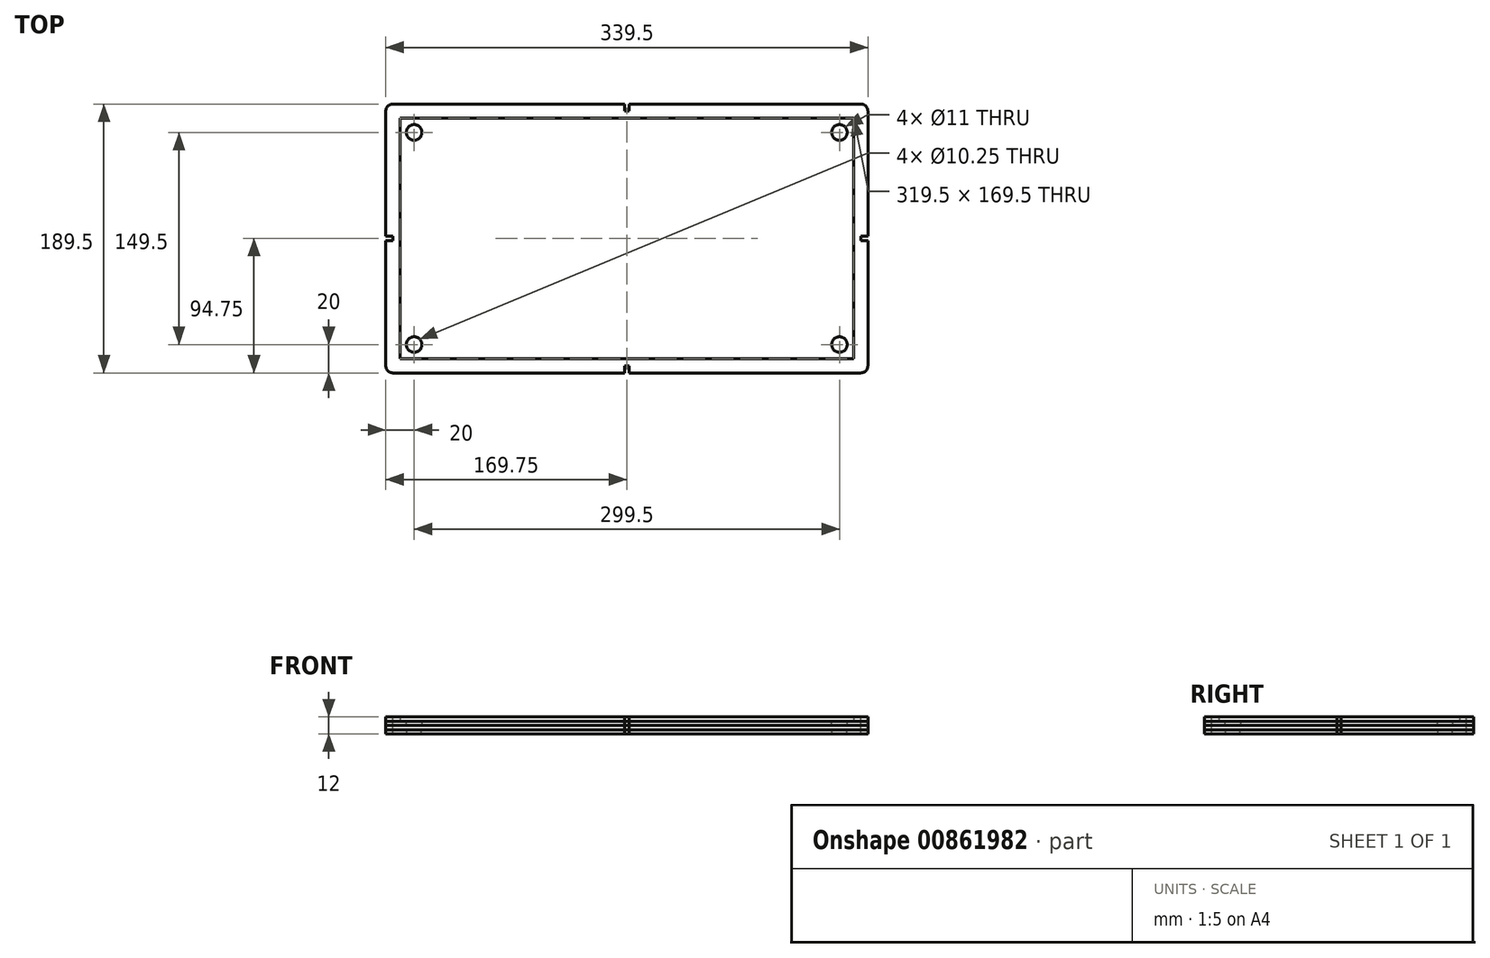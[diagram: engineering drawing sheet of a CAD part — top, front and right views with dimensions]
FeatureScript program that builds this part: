
annotation { "Feature Type Name" : "Feature", "Feature Type Description" : "" }
export const myFeature = defineFeature(function(context is Context, id is Id, definition is map)
    precondition{}
    {
        {
            var Q0;
            Q0=qCreatedBy(makeId("Top.planeOp"),FACE);
            var sketch = newSketch(context, id + "F0", { "sketchPlane" : qUnion([Q0])});
            skLineSegment(sketch, "E0.bottom", {"start": v(-158.75, 83.75) * mm, "end": v(158.75, 83.75) * mm});
            skLineSegment(sketch, "E0.top", {"start": v(-158.75, -83.75) * mm, "end": v(158.75, -83.75) * mm});
            skLineSegment(sketch, "E0.left", {"start": v(-158.75, 83.75) * mm, "end": v(-158.75, -83.75) * mm});
            skLineSegment(sketch, "E0.right", {"start": v(158.75, 83.75) * mm, "end": v(158.75, -83.75) * mm});
            skPoint(sketch, "E0.middle", {"position": v(0, 0) * mm});
            skLineSegment(sketch, "E1.bottom", {"start": v(-149.75, 74.75) * mm, "end": v(149.75, 74.75) * mm, "construction": true});
            skLineSegment(sketch, "E1.top", {"start": v(-149.75, -74.75) * mm, "end": v(149.75, -74.75) * mm, "construction": true});
            skLineSegment(sketch, "E1.left", {"start": v(-149.75, 74.75) * mm, "end": v(-149.75, -74.75) * mm, "construction": true});
            skLineSegment(sketch, "E1.right", {"start": v(149.75, 74.75) * mm, "end": v(149.75, -74.75) * mm, "construction": true});
            skCircle(sketch, "E2", {"center": v(-149.75, 74.75) * mm, "radius": 6 * mm});
            skCircle(sketch, "E3", {"center": v(149.75, 74.75) * mm, "radius": 6 * mm});
            skCircle(sketch, "E4", {"center": v(149.75, -74.75) * mm, "radius": 6 * mm});
            skCircle(sketch, "E5", {"center": v(-149.75, -74.75) * mm, "radius": 6 * mm});
            skSolve(sketch);
        }
        {
            var Q0;
            Q0=makeQuery(id+"F0.imprint","IMPRINT",FACE,{"disambiguationData":[TD([[makeQuery(id+"F0.imprint","IMPRINT",EDGE,{"derivedFrom":sQuery(id+"F0.wireOp",EDGE,"E0.bottom")}),-1.0]])]});
            var sketch = newSketch(context, id + "F1", { "sketchPlane" : qUnion([Q0])});
            skLineSegment(sketch, "E6.0", {"start": v(-159.75, 84.75) * mm, "end": v(-159.75, -84.75) * mm});
            skLineSegment(sketch, "E6.1", {"start": v(159.75, 84.75) * mm, "end": v(-159.75, 84.75) * mm});
            skLineSegment(sketch, "E6.2", {"start": v(159.75, -84.75) * mm, "end": v(159.75, 84.75) * mm});
            skLineSegment(sketch, "E6.3", {"start": v(-159.75, -84.75) * mm, "end": v(159.75, -84.75) * mm});
            skLineSegment(sketch, "E7.bottom", {"start": v(164.75, 94.75) * mm, "end": v(-164.75, 94.75) * mm});
            skLineSegment(sketch, "E7.top", {"start": v(164.75, -94.75) * mm, "end": v(-164.75, -94.75) * mm});
            skLineSegment(sketch, "E7.left", {"start": v(169.75, 89.75) * mm, "end": v(169.75, -89.75) * mm});
            skLineSegment(sketch, "E7.right", {"start": v(-169.75, 89.75) * mm, "end": v(-169.75, -89.75) * mm});
            skPoint(sketch, "E7.middle", {"position": v(0, 0) * mm});
            skPoint(sketch, "E8.visualSharp", {"position": v(169.75, 94.75) * mm});
            skArc(sketch, "E8.filletArc", {"start": v(169.75, 89.75) * mm, "mid": v(168.29, 93.29) * mm, "end": v(164.75, 94.75) * mm});
            skPoint(sketch, "E9.visualSharp", {"position": v(169.75, -94.75) * mm});
            skArc(sketch, "E9.filletArc", {"start": v(164.75, -94.75) * mm, "mid": v(168.29, -93.29) * mm, "end": v(169.75, -89.75) * mm});
            skPoint(sketch, "E10.visualSharp", {"position": v(-169.75, -94.75) * mm});
            skArc(sketch, "E10.filletArc", {"start": v(-169.75, -89.75) * mm, "mid": v(-168.29, -93.29) * mm, "end": v(-164.75, -94.75) * mm});
            skPoint(sketch, "E11.visualSharp", {"position": v(-169.75, 94.75) * mm});
            skArc(sketch, "E11.filletArc", {"start": v(-164.75, 94.75) * mm, "mid": v(-168.29, 93.29) * mm, "end": v(-169.75, 89.75) * mm});
            skSolve(sketch);
        }
        {
            var Q0;
            Q0 = qSketchRegion(id + "F1", true);
            extrude(context, id + "F2", {"entities" : qUnion([Q0]), "depth" : 3 * mm, "offsetDistance" : 25 * mm});
        }
        {
            var Q0;
            Q0=makeQuery(id+"F2.opExtrude","CAP_FACE",FACE,{"disambiguationData":[OSD([sQuery(id+"F1.wireOp",EDGE,"E6.0"),sQuery(id+"F1.wireOp",EDGE,"E6.1"),sQuery(id+"F1.wireOp",EDGE,"E6.2"),sQuery(id+"F1.wireOp",EDGE,"E6.3"),sQuery(id+"F1.wireOp",EDGE,"E7.bottom"),sQuery(id+"F1.wireOp",EDGE,"E7.top"),sQuery(id+"F1.wireOp",EDGE,"E7.left"),sQuery(id+"F1.wireOp",EDGE,"E7.right"),sQuery(id+"F1.wireOp",EDGE,"E8.filletArc"),sQuery(id+"F1.wireOp",EDGE,"E9.filletArc"),sQuery(id+"F1.wireOp",EDGE,"E10.filletArc"),sQuery(id+"F1.wireOp",EDGE,"E11.filletArc")])],"isStart":true});
            var sketch = newSketch(context, id + "F3", { "sketchPlane" : qUnion([Q0])});
            skLineSegment(sketch, "E12.0.0", {"start": v(164.75, 94.75) * mm, "end": v(-164.75, 94.75) * mm});
            skArc(sketch, "E12.0.1", {"start": v(-164.75, 94.75) * mm, "mid": v(-168.29, 93.29) * mm, "end": v(-169.75, 89.75) * mm});
            skLineSegment(sketch, "E12.0.2", {"start": v(-169.75, 89.75) * mm, "end": v(-169.75, -89.75) * mm});
            skArc(sketch, "E12.0.3", {"start": v(-169.75, -89.75) * mm, "mid": v(-168.29, -93.29) * mm, "end": v(-164.75, -94.75) * mm});
            skLineSegment(sketch, "E12.0.4", {"start": v(-164.75, -94.75) * mm, "end": v(164.75, -94.75) * mm});
            skArc(sketch, "E12.0.5", {"start": v(164.75, -94.75) * mm, "mid": v(168.29, -93.29) * mm, "end": v(169.75, -89.75) * mm});
            skLineSegment(sketch, "E12.0.6", {"start": v(169.75, -89.75) * mm, "end": v(169.75, 89.75) * mm});
            skArc(sketch, "E12.0.7", {"start": v(169.75, 89.75) * mm, "mid": v(168.29, 93.29) * mm, "end": v(164.75, 94.75) * mm});
            skCircle(sketch, "E13.0", {"center": v(-149.75, 74.75) * mm, "radius": 5.5 * mm});
            skCircle(sketch, "E14.0", {"center": v(149.75, 74.75) * mm, "radius": 5.5 * mm});
            skCircle(sketch, "E15.0", {"center": v(149.75, -74.75) * mm, "radius": 5.5 * mm});
            skCircle(sketch, "E16.0", {"center": v(-149.75, -74.75) * mm, "radius": 5.5 * mm});
            skSolve(sketch);
        }
        {
            var Q0;
            Q0 = qSketchRegion(id + "F3", true);
            extrude(context, id + "F4", {"entities" : qUnion([Q0]), "depth" : 3 * mm, "offsetDistance" : 25 * mm});
        }
        {
            var Q0;
            Q0=makeQuery(id+"F4.opExtrude","CAP_FACE",FACE,{"disambiguationData":[OSD([sQuery(id+"F3.wireOp",EDGE,"E12.0.0"),sQuery(id+"F3.wireOp",EDGE,"E12.0.1"),sQuery(id+"F3.wireOp",EDGE,"E12.0.2"),sQuery(id+"F3.wireOp",EDGE,"E12.0.3"),sQuery(id+"F3.wireOp",EDGE,"E12.0.4"),sQuery(id+"F3.wireOp",EDGE,"E12.0.5"),sQuery(id+"F3.wireOp",EDGE,"E12.0.6"),sQuery(id+"F3.wireOp",EDGE,"E12.0.7"),sQuery(id+"F3.wireOp",EDGE,"E13.0"),sQuery(id+"F3.wireOp",EDGE,"E14.0"),sQuery(id+"F3.wireOp",EDGE,"E15.0"),sQuery(id+"F3.wireOp",EDGE,"E16.0")])],"isStart":false});
            var sketch = newSketch(context, id + "F5", { "sketchPlane" : qUnion([Q0])});
            skArc(sketch, "E17.0.0", {"start": v(169.75, 89.75) * mm, "mid": v(168.29, 93.29) * mm, "end": v(164.75, 94.75) * mm});
            skLineSegment(sketch, "E17.0.1", {"start": v(164.75, 94.75) * mm, "end": v(-164.75, 94.75) * mm});
            skArc(sketch, "E17.0.2", {"start": v(-164.75, 94.75) * mm, "mid": v(-168.29, 93.29) * mm, "end": v(-169.75, 89.75) * mm});
            skLineSegment(sketch, "E17.0.3", {"start": v(-169.75, 89.75) * mm, "end": v(-169.75, -89.75) * mm});
            skArc(sketch, "E17.0.4", {"start": v(-169.75, -89.75) * mm, "mid": v(-168.29, -93.29) * mm, "end": v(-164.75, -94.75) * mm});
            skLineSegment(sketch, "E17.0.5", {"start": v(-164.75, -94.75) * mm, "end": v(164.75, -94.75) * mm});
            skArc(sketch, "E17.0.6", {"start": v(164.75, -94.75) * mm, "mid": v(168.29, -93.29) * mm, "end": v(169.75, -89.75) * mm});
            skLineSegment(sketch, "E17.0.7", {"start": v(169.75, -89.75) * mm, "end": v(169.75, 89.75) * mm});
            skSolve(sketch);
        }
        {
            var Q0;
            Q0 = qSketchRegion(id + "F5", true);
            extrude(context, id + "F6", {"entities" : qUnion([Q0]), "depth" : 3 * mm, "offsetDistance" : 25 * mm});
        }
        {
            var Q0;
            Q0=makeQuery(id+"F6.opExtrude","CAP_FACE",FACE,{"disambiguationData":[OSD([sQuery(id+"F5.wireOp",EDGE,"E17.0.0"),sQuery(id+"F5.wireOp",EDGE,"E17.0.1"),sQuery(id+"F5.wireOp",EDGE,"E17.0.2"),sQuery(id+"F5.wireOp",EDGE,"E17.0.3"),sQuery(id+"F5.wireOp",EDGE,"E17.0.4"),sQuery(id+"F5.wireOp",EDGE,"E17.0.5"),sQuery(id+"F5.wireOp",EDGE,"E17.0.6"),sQuery(id+"F5.wireOp",EDGE,"E17.0.7")])],"isStart":false});
            var sketch = newSketch(context, id + "F7", { "sketchPlane" : qUnion([Q0])});
            skArc(sketch, "E18.0.0", {"start": v(169.75, 89.75) * mm, "mid": v(168.29, 93.29) * mm, "end": v(164.75, 94.75) * mm});
            skLineSegment(sketch, "E18.0.1", {"start": v(164.75, 94.75) * mm, "end": v(-164.75, 94.75) * mm});
            skArc(sketch, "E18.0.2", {"start": v(-164.75, 94.75) * mm, "mid": v(-168.29, 93.29) * mm, "end": v(-169.75, 89.75) * mm});
            skLineSegment(sketch, "E18.0.3", {"start": v(-169.75, 89.75) * mm, "end": v(-169.75, -89.75) * mm});
            skArc(sketch, "E18.0.4", {"start": v(-169.75, -89.75) * mm, "mid": v(-168.29, -93.29) * mm, "end": v(-164.75, -94.75) * mm});
            skLineSegment(sketch, "E18.0.5", {"start": v(-164.75, -94.75) * mm, "end": v(164.75, -94.75) * mm});
            skArc(sketch, "E18.0.6", {"start": v(164.75, -94.75) * mm, "mid": v(168.29, -93.29) * mm, "end": v(169.75, -89.75) * mm});
            skLineSegment(sketch, "E18.0.7", {"start": v(169.75, -89.75) * mm, "end": v(169.75, 89.75) * mm});
            skCircle(sketch, "E19.0", {"center": v(149.75, -74.75) * mm, "radius": 5.5 * mm, "construction": true});
            skCircle(sketch, "E20.0", {"center": v(-149.75, -74.75) * mm, "radius": 5.5 * mm, "construction": true});
            skCircle(sketch, "E21.0", {"center": v(-149.75, 74.75) * mm, "radius": 5.5 * mm, "construction": true});
            skCircle(sketch, "E22.0", {"center": v(149.75, 74.75) * mm, "radius": 5.5 * mm, "construction": true});
            skCircle(sketch, "E23", {"center": v(-149.75, 74.75) * mm, "radius": 5.12 * mm});
            skCircle(sketch, "E24", {"center": v(149.75, 74.75) * mm, "radius": 5.12 * mm});
            skCircle(sketch, "E25", {"center": v(149.75, -74.75) * mm, "radius": 5.12 * mm});
            skCircle(sketch, "E26", {"center": v(-149.75, -74.75) * mm, "radius": 5.12 * mm});
            skSolve(sketch);
        }
        {
            var Q0;
            Q0 = qSketchRegion(id + "F7", true);
            extrude(context, id + "F8", {"entities" : qUnion([Q0]), "depth" : 3 * mm, "offsetDistance" : 25 * mm});
        }
        {
            var Q0;
            Q0=makeQuery(id+"F2.opExtrude","CAP_FACE",FACE,{"disambiguationData":[OSD([sQuery(id+"F1.wireOp",EDGE,"E6.0"),sQuery(id+"F1.wireOp",EDGE,"E6.1"),sQuery(id+"F1.wireOp",EDGE,"E6.2"),sQuery(id+"F1.wireOp",EDGE,"E6.3"),sQuery(id+"F1.wireOp",EDGE,"E7.bottom"),sQuery(id+"F1.wireOp",EDGE,"E7.top"),sQuery(id+"F1.wireOp",EDGE,"E7.left"),sQuery(id+"F1.wireOp",EDGE,"E7.right"),sQuery(id+"F1.wireOp",EDGE,"E8.filletArc"),sQuery(id+"F1.wireOp",EDGE,"E9.filletArc"),sQuery(id+"F1.wireOp",EDGE,"E10.filletArc"),sQuery(id+"F1.wireOp",EDGE,"E11.filletArc")])],"isStart":false});
            var sketch = newSketch(context, id + "F9", { "sketchPlane" : qUnion([Q0])});
            skPoint(sketch, "E27.endSnap0", {"position": v(0, 84.75) * mm});
            skLineSegment(sketch, "E28.bottom", {"start": v(-1.5, 94.75) * mm, "end": v(1.5, 94.75) * mm});
            skLineSegment(sketch, "E28.top", {"start": v(-1.5, 89.75) * mm, "end": v(1.5, 89.75) * mm});
            skLineSegment(sketch, "E28.left", {"start": v(-1.5, 94.75) * mm, "end": v(-1.5, 89.75) * mm});
            skLineSegment(sketch, "E28.right", {"start": v(1.5, 94.75) * mm, "end": v(1.5, 89.75) * mm});
            skLineSegment(sketch, "E29", {"start": v(0, 89.75) * mm, "end": v(0, 94.75) * mm, "construction": true});
            skLineSegment(sketch, "E30", {"start": v(0, 0) * mm, "end": v(0, 84.75) * mm, "construction": true});
            skLineSegment(sketch, "E31", {"start": v(0, 0) * mm, "end": v(169.75, 0) * mm, "construction": true});
            skLineSegment(sketch, "E32.MirrorCS", {"start": v(1.5, 89.75) * mm, "end": v(-1.5, 89.75) * mm});
            skLineSegment(sketch, "E33.MirrorCS", {"start": v(1.5, 94.75) * mm, "end": v(-1.5, 94.75) * mm});
            skLineSegment(sketch, "E34.MirrorCS", {"start": v(1.5, -94.75) * mm, "end": v(-1.5, -94.75) * mm});
            skLineSegment(sketch, "E35.MirrorCS", {"start": v(1.5, -89.75) * mm, "end": v(-1.5, -89.75) * mm});
            skLineSegment(sketch, "E36.MirrorCS", {"start": v(-1.5, -94.75) * mm, "end": v(1.5, -94.75) * mm});
            skLineSegment(sketch, "E37.MirrorCS", {"start": v(1.5, -94.75) * mm, "end": v(1.5, -89.75) * mm});
            skLineSegment(sketch, "E38.MirrorCS", {"start": v(-1.5, -89.75) * mm, "end": v(1.5, -89.75) * mm});
            skLineSegment(sketch, "E39.MirrorCS", {"start": v(-1.5, -94.75) * mm, "end": v(-1.5, -89.75) * mm});
            skLineSegment(sketch, "E40.MirrorCS", {"start": v(0, -89.75) * mm, "end": v(0, -94.75) * mm, "construction": true});
            skLineSegment(sketch, "E41.bottom", {"start": v(169.75, -1.5) * mm, "end": v(164.75, -1.5) * mm});
            skLineSegment(sketch, "E41.top", {"start": v(169.75, 1.5) * mm, "end": v(164.75, 1.5) * mm});
            skLineSegment(sketch, "E41.left", {"start": v(169.75, -1.5) * mm, "end": v(169.75, 1.5) * mm});
            skLineSegment(sketch, "E41.right", {"start": v(164.75, -1.5) * mm, "end": v(164.75, 1.5) * mm});
            skPoint(sketch, "E42", {"position": v(164.75, 0) * mm});
            skLineSegment(sketch, "E43.MirrorCS", {"start": v(-169.75, -1.5) * mm, "end": v(-169.75, 1.5) * mm});
            skLineSegment(sketch, "E44.MirrorCS", {"start": v(-164.75, -1.5) * mm, "end": v(-164.75, 1.5) * mm});
            skLineSegment(sketch, "E45.MirrorCS", {"start": v(-169.75, 1.5) * mm, "end": v(-164.75, 1.5) * mm});
            skLineSegment(sketch, "E46.MirrorCS", {"start": v(-169.75, -1.5) * mm, "end": v(-164.75, -1.5) * mm});
            skLineSegment(sketch, "E47.MirrorCS", {"start": v(0, 0) * mm, "end": v(-169.75, 0) * mm, "construction": true});
            skPoint(sketch, "E48.MirrorP", {"position": v(-164.75, 0) * mm});
            skSolve(sketch);
        }
        {
            var Q0;
            Q0 = qSketchRegion(id + "F9", true);
            extrude(context, id + "F10", {"entities" : qUnion([Q0]), "operationType" : NewBodyOperationType.REMOVE, "endBound" : BoundingType.THROUGH_ALL, "oppositeDirection" : true, "depth" : 25 * mm, "offsetDistance" : 25 * mm});
        }
    });
